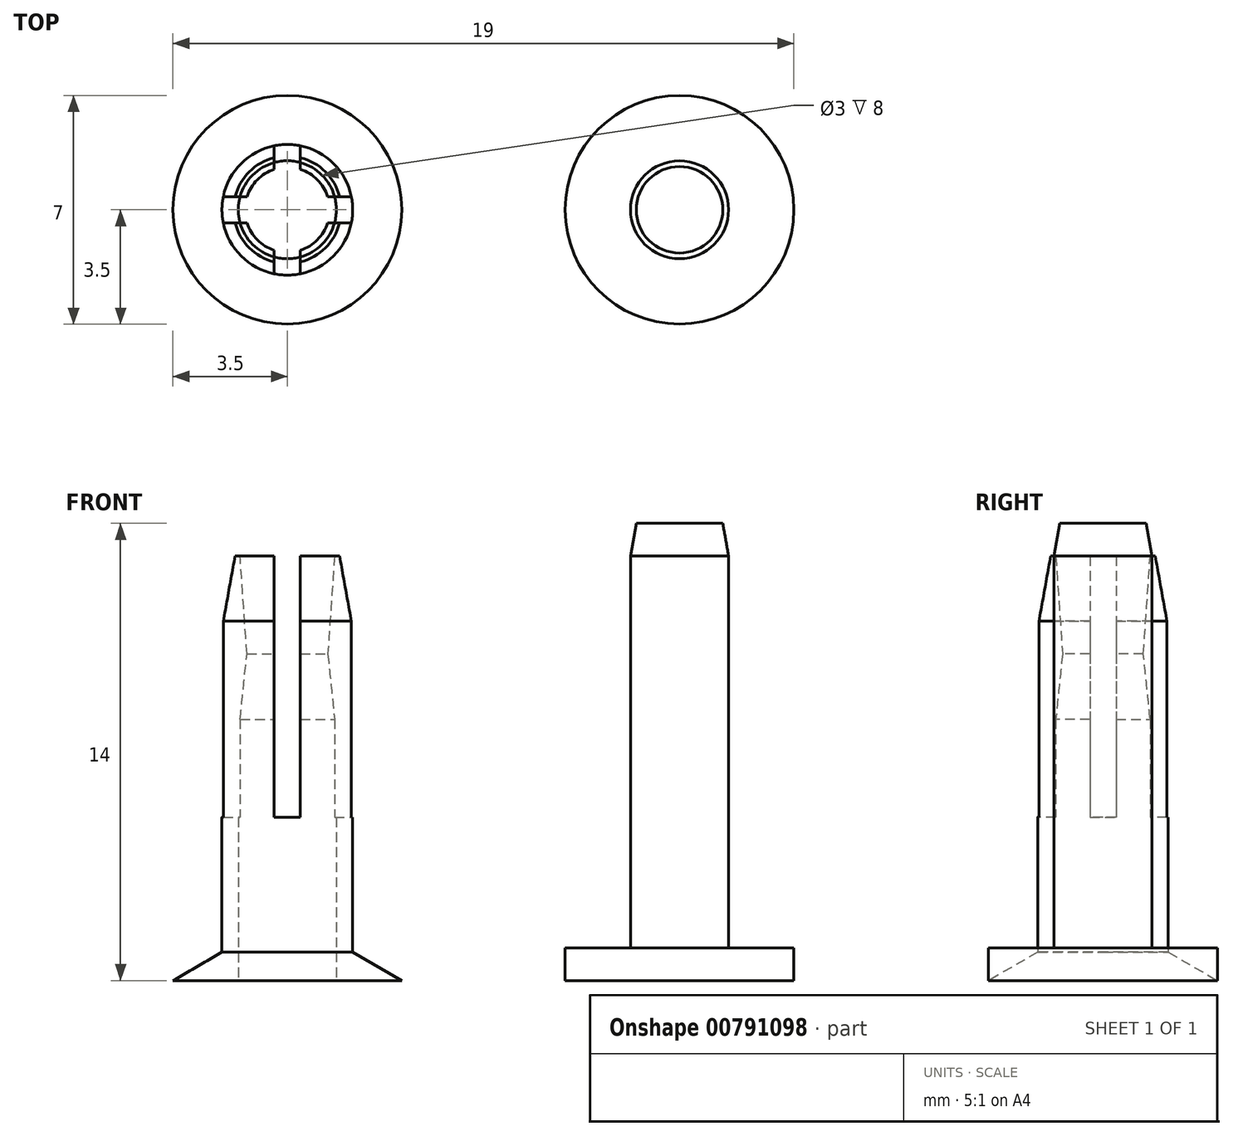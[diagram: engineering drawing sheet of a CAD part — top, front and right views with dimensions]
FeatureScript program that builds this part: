
annotation { "Feature Type Name" : "Feature", "Feature Type Description" : "" }
export const myFeature = defineFeature(function(context is Context, id is Id, definition is map)
    precondition{}
    {
        {
            var Q0;
            Q0=qCreatedBy(makeId("Top.planeOp"),FACE);
            var sketch = newSketch(context, id + "F0", { "sketchPlane" : qUnion([Q0])});
            skCircle(sketch, "E0", {"center": v(-6, 0) * mm, "radius": 3.5 * mm});
            skCircle(sketch, "E1", {"center": v(6, 0) * mm, "radius": 3.5 * mm});
            skSolve(sketch);
        }
        {
            var Q0;
            Q0=makeQuery(id+"F0.imprint","IMPRINT",FACE,{"disambiguationData":[TD([[makeQuery(id+"F0.imprint","IMPRINT",EDGE,{"derivedFrom":sQuery(id+"F0.wireOp",EDGE,"E0")}),1.0]])]});
            var Q1;
            Q1=makeQuery(id+"F0.imprint","IMPRINT",FACE,{"disambiguationData":[TD([[makeQuery(id+"F0.imprint","IMPRINT",EDGE,{"derivedFrom":sQuery(id+"F0.wireOp",EDGE,"E1")}),1.0]])]});
            extrude(context, id + "F1", {"entities" : qUnion([Q0, Q1]), "depth" : 1 * mm, "offsetDistance" : 25 * mm});
        }
        {
            var Q0;
            Q0=makeQuery(id+"F1.opExtrude","CAP_EDGE",EDGE,{"disambiguationData":[OSD([sQuery(id+"F0.wireOp",EDGE,"E0")])],"isStart":false});
            chamfer(context, id + "F2", {"entities" : qUnion([Q0]), "chamferType" : ChamferType.OFFSET_ANGLE, "width" : 1 * mm, "oppositeDirection" : true, "angle" : 60 * degree, "tangentPropagation" : true});
        }
        {
            var Q0;
            Q0=qCreatedBy(makeId("Top.planeOp"),FACE);
            var sketch = newSketch(context, id + "F3", { "sketchPlane" : qUnion([Q0])});
            skCircle(sketch, "E2", {"center": v(-6, 0) * mm, "radius": 2 * mm});
            skSolve(sketch);
        }
        {
            var Q0;
            Q0 = qSketchRegion(id + "F3", true);
            extrude(context, id + "F4", {"entities" : qUnion([Q0]), "operationType" : NewBodyOperationType.ADD, "depth" : 13 * mm, "offsetDistance" : 25 * mm});
        }
        {
            var Q0;
            Q0=makeQuery(id+"F4.opExtrude","CAP_EDGE",EDGE,{"disambiguationData":[OSD([sQuery(id+"F3.wireOp",EDGE,"E2")])],"isStart":false});
            chamfer(context, id + "F5", {"entities" : qUnion([Q0]), "chamferType" : ChamferType.OFFSET_ANGLE, "width" : 2 * mm, "oppositeDirection" : true, "angle" : 10 * degree, "tangentPropagation" : true});
        }
        {
            var Q0;
            Q0=qCreatedBy(makeId("Front.planeOp"),FACE);
            var sketch = newSketch(context, id + "F6", { "sketchPlane" : qUnion([Q0])});
            skLineSegment(sketch, "E3", {"start": v(-6, 13) * mm, "end": v(-6, 0) * mm});
            skLineSegment(sketch, "E4", {"start": v(-6, 0) * mm, "end": v(-4.5, 0) * mm});
            skLineSegment(sketch, "E5", {"start": v(-4.5, 0) * mm, "end": v(-4.5, 8) * mm});
            skLineSegment(sketch, "E6", {"start": v(-4.5, 8) * mm, "end": v(-4.7, 10) * mm});
            skLineSegment(sketch, "E7", {"start": v(-4.7, 10) * mm, "end": v(-4.5, 13) * mm});
            skLineSegment(sketch, "E8", {"start": v(-4.5, 13) * mm, "end": v(-6, 13) * mm});
            skSolve(sketch);
        }
        {
            var Q0;
            Q0 = qSketchRegion(id + "F6", true);
            var Q1;
            Q1=sQuery(id+"F6.wireOp",EDGE,"E3");
            revolve(context, id + "F7", {"operationType" : NewBodyOperationType.REMOVE, "surfaceOperationType" : NewSurfaceOperationType.NEW, "entities" : qUnion([Q0]), "axis" : qUnion([Q1]), "revolveType" : RevolveType.FULL, "oppositeDirection" : true});
        }
        {
            var Q0;
            Q0=makeQuery(id+"F1.opExtrude","CAP_FACE",FACE,{"disambiguationData":[OSD([sQuery(id+"F0.wireOp",EDGE,"E1")])],"isStart":false});
            var sketch = newSketch(context, id + "F8", { "sketchPlane" : qUnion([Q0])});
            skCircle(sketch, "E9", {"center": v(6, 0) * mm, "radius": 1.5 * mm});
            skSolve(sketch);
        }
        {
            var Q0;
            Q0=makeQuery(id+"F8.imprint","IMPRINT",FACE,{"disambiguationData":[TD([[makeQuery(id+"F8.imprint","IMPRINT",EDGE,{"derivedFrom":sQuery(id+"F8.wireOp",EDGE,"E9")}),1.0]])]});
            extrude(context, id + "F9", {"entities" : qUnion([Q0]), "operationType" : NewBodyOperationType.ADD, "depth" : 13 * mm, "offsetDistance" : 25 * mm});
        }
        {
            var Q0;
            Q0=makeQuery(id+"F9.opExtrude","CAP_EDGE",EDGE,{"disambiguationData":[OSD([sQuery(id+"F8.wireOp",EDGE,"E9")])],"isStart":false});
            chamfer(context, id + "F10", {"entities" : qUnion([Q0]), "chamferType" : ChamferType.OFFSET_ANGLE, "width" : 1 * mm, "oppositeDirection" : true, "angle" : 10 * degree, "tangentPropagation" : true});
        }
        {
            var Q0;
            Q0=makeQuery(id+"F4.opExtrude","CAP_FACE",FACE,{"disambiguationData":[OSD([sQuery(id+"F3.wireOp",EDGE,"E2")])],"isStart":false});
            var sketch = newSketch(context, id + "F11", { "sketchPlane" : qUnion([Q0])});
            skLineSegment(sketch, "E10.bottom", {"start": v(-8.5, 0.4) * mm, "end": v(-3.5, 0.4) * mm});
            skLineSegment(sketch, "E10.top", {"start": v(-8.5, -0.4) * mm, "end": v(-3.5, -0.4) * mm});
            skLineSegment(sketch, "E10.left", {"start": v(-8.5, 0.4) * mm, "end": v(-8.5, -0.4) * mm});
            skLineSegment(sketch, "E10.right", {"start": v(-3.5, 0.4) * mm, "end": v(-3.5, -0.4) * mm});
            skLineSegment(sketch, "E11.bottom", {"start": v(-6.4, 2.5) * mm, "end": v(-5.6, 2.5) * mm});
            skLineSegment(sketch, "E11.top", {"start": v(-6.4, -2.5) * mm, "end": v(-5.6, -2.5) * mm});
            skLineSegment(sketch, "E11.left", {"start": v(-6.4, 2.5) * mm, "end": v(-6.4, -2.5) * mm});
            skLineSegment(sketch, "E11.right", {"start": v(-5.6, 2.5) * mm, "end": v(-5.6, -2.5) * mm});
            skSolve(sketch);
        }
        {
            var Q0;
            Q0 = qSketchRegion(id + "F11", true);
            extrude(context, id + "F12", {"entities" : qUnion([Q0]), "operationType" : NewBodyOperationType.REMOVE, "oppositeDirection" : true, "depth" : 8 * mm, "offsetDistance" : 25 * mm});
        }
    });
